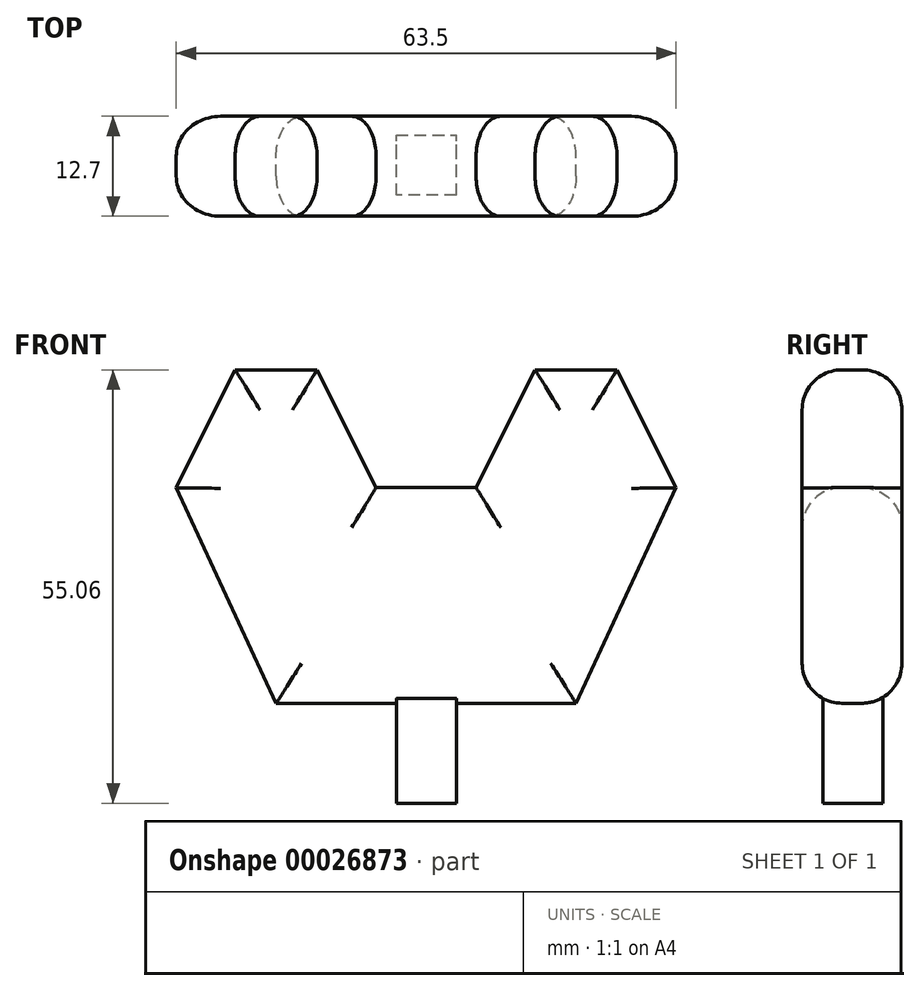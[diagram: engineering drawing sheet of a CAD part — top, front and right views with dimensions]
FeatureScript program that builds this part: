
annotation { "Feature Type Name" : "Feature", "Feature Type Description" : "" }
export const myFeature = defineFeature(function(context is Context, id is Id, definition is map)
    precondition{}
    {
        {
            var Q0;
            Q0=qCreatedBy(makeId("Front.planeOp"),FACE);
            var sketch = newSketch(context, id + "F0", { "sketchPlane" : qUnion([Q0])});
            skLineSegment(sketch, "E0.bottom", {"start": v(-25.8, 42.01) * mm, "end": v(-13.1, 42.01) * mm});
            skLineSegment(sketch, "E0.top", {"start": v(-38.5, 14.63) * mm, "end": v(-0.4, 14.63) * mm});
            skLineSegment(sketch, "E1", {"start": v(-5.6, 57) * mm, "end": v(-13.1, 42.01) * mm});
            skLineSegment(sketch, "E2", {"start": v(4.81, 57) * mm, "end": v(12.3, 42.01) * mm});
            skLineSegment(sketch, "E3", {"start": v(-25.8, 42.01) * mm, "end": v(-33.29, 57) * mm});
            skLineSegment(sketch, "E4", {"start": v(-43.7, 57) * mm, "end": v(-51.2, 42.01) * mm});
            skLineSegment(sketch, "E5", {"start": v(-43.7, 57) * mm, "end": v(-33.29, 57) * mm});
            skPoint(sketch, "E6.orphan", {"position": v(-0.4, 67.41) * mm});
            skPoint(sketch, "E7.left.end.orphan", {"position": v(12.3, 67.41) * mm});
            skPoint(sketch, "E8.orphan", {"position": v(-13.1, 67.41) * mm});
            skLineSegment(sketch, "E9.trimOffspring", {"start": v(-5.6, 57) * mm, "end": v(4.81, 57) * mm});
            skPoint(sketch, "E10.orphan", {"position": v(-25.8, 67.41) * mm});
            skPoint(sketch, "E11.orphan", {"position": v(-38.5, 67.41) * mm});
            skPoint(sketch, "E12.left.end.orphan", {"position": v(-51.2, 67.41) * mm});
            skLineSegment(sketch, "E13", {"start": v(-51.2, 42.01) * mm, "end": v(-38.5, 14.63) * mm});
            skLineSegment(sketch, "E14", {"start": v(12.3, 42.01) * mm, "end": v(-0.4, 14.63) * mm});
            skPoint(sketch, "E15.orphan", {"position": v(12.3, 14.63) * mm});
            skPoint(sketch, "E0.left.end.orphan", {"position": v(-51.2, 14.63) * mm});
            skSolve(sketch);
        }
        {
            var Q0;
            Q0 = qSketchRegion(id + "F0", true);
            extrude(context, id + "F1", {"entities" : qUnion([Q0]), "depth" : 12.7 * mm});
        }
        {
            var Q0;
            Q0=makeQuery(id+"F1.opExtrude","SWEPT_FACE",FACE,{"disambiguationData":[OSD([sQuery(id+"F0.wireOp",EDGE,"E0.top")])]});
            var sketch = newSketch(context, id + "F2", { "sketchPlane" : qUnion([Q0])});
            skLineSegment(sketch, "E16.bottom", {"start": v(-23.24, 10.03) * mm, "end": v(-15.62, 10.03) * mm});
            skLineSegment(sketch, "E16.top", {"start": v(-23.24, 2.4) * mm, "end": v(-15.62, 2.4) * mm});
            skLineSegment(sketch, "E16.left", {"start": v(-23.24, 10.03) * mm, "end": v(-23.24, 2.4) * mm});
            skLineSegment(sketch, "E16.right", {"start": v(-15.62, 10.03) * mm, "end": v(-15.62, 2.4) * mm});
            skSolve(sketch);
        }
        {
            var Q0;
            Q0 = qSketchRegion(id + "F2", true);
            extrude(context, id + "F3", {"entities" : qUnion([Q0]), "operationType" : NewBodyOperationType.ADD, "depth" : 12.7 * mm});
        }
        {
            var Q0;
            Q0=makeQuery(id+"F1.opExtrude","CAP_FACE",FACE,{"disambiguationData":[OSD([sQuery(id+"F0.wireOp",EDGE,"E0.bottom"),sQuery(id+"F0.wireOp",EDGE,"E0.top"),sQuery(id+"F0.wireOp",EDGE,"E1"),sQuery(id+"F0.wireOp",EDGE,"E2"),sQuery(id+"F0.wireOp",EDGE,"E3"),sQuery(id+"F0.wireOp",EDGE,"E4"),sQuery(id+"F0.wireOp",EDGE,"E5"),sQuery(id+"F0.wireOp",EDGE,"E9.trimOffspring"),sQuery(id+"F0.wireOp",EDGE,"E13"),sQuery(id+"F0.wireOp",EDGE,"E14")])],"isStart":false});
            var Q1;
            Q1=makeQuery(id+"F1.opExtrude","CAP_FACE",FACE,{"disambiguationData":[OSD([sQuery(id+"F0.wireOp",EDGE,"E0.bottom"),sQuery(id+"F0.wireOp",EDGE,"E0.top"),sQuery(id+"F0.wireOp",EDGE,"E1"),sQuery(id+"F0.wireOp",EDGE,"E2"),sQuery(id+"F0.wireOp",EDGE,"E3"),sQuery(id+"F0.wireOp",EDGE,"E4"),sQuery(id+"F0.wireOp",EDGE,"E5"),sQuery(id+"F0.wireOp",EDGE,"E9.trimOffspring"),sQuery(id+"F0.wireOp",EDGE,"E13"),sQuery(id+"F0.wireOp",EDGE,"E14")])],"isStart":true});
            fillet(context, id + "F4", {"entities" : qUnion([Q0, Q1]), "radius" : 5.08 * mm, "tangentPropagation" : true, "allowEdgeOverflow" : false});
        }
    });
